# Revit family: UNB_Specchio_Multiproduct_BIM_IT_T3339;T3340;T3341;T3342;T3343;T3344_NEW
name_source: partatom
category: Plumbing Fixtures
revit_build: Autodesk Revit 2017 (Build: 20160225_1515(x64)
units: mm (PartAtom-declared; Revit-internal decimal feet)

## family parameters
Cut with Voids When Loaded = No
Host = Face
Part Type = Normal
Room Calculation Point = No
Round Connector Dimension = Use Diameter
Shared = No

## types (6) — shared parameters
Accessori = http://www.idealstandard.it
AltezzaNominale = 700 mm  [stored 2.29659 ft]
Autore = Ideal Standard
Brand = Ideal Standard
CodiceDiPrestazione = EN
Colore = specchio
Connessione = piombatura
Default Elevation = 1500 mm  [stored 4.92126 ft]
DescrizioneClassifcazioneUni2015 = Bathroom furniture
Finitura = specchio
Forma = rettangolare
Garanzia = garanzia del produttore
IfcEsportaCome = BATHROOM FURNITURE
InformazioniDiProdotto = http://www.idealstandard.it
InstruzioniInstallazione = http://www.idealstandard.it
LunghezzaNominale = 26 mm
Materiale = bicchiere
PartiDiRicambio = http://www.idealstandard.it
ProfonditàNominale = 26 mm
Revisione = 1
RiferimentoClassificazioneUni2015 = MIRRORS
Spazio = interno
Telefono = 800 652 290
TipoDiDato = Fisso
TipoEspotazioneIfc = IfcFurnitureType
TipologiaVaso = Altro
URL = http://www.idealstandard.it
UnitàDurata = anno
UnitàDurataGaranzia = anno
UnitàLineare = millimetro
UnitàMonetaria = €
UnitàSuperficie = millimetro
UnitàVolume = litro
Versione = 1
VersioneClassificazioneUni2015 = IfcFurnitureType
zero-valued in all types: Cost, CostoDiSostituzione

## per-type parameters (varying)
| type | Caratteristiche | CodiceABarre | Description | LarghezzaNominale | Model | ModelloDiRiferimento | Nome | NomeOggettoBim | NumeroDiModello | PesoNetto | Riferimento |
| T3341 - 700 x 700 mirror | SPECCHIO MID LIGHT 70X70 29,3W 230W | 8014140447337 | SPECCHIO MID LIGHT 70X70 29,3W 230W | 700 mm  [stored 2.29659 ft] | T3341BH | SPECCHIO MID LIGHT 70X70 29,3W 230W | ISI_IdealStandard_Specchio_T3341 | ISI_IdealStandard_Specchio_T3341 | T3341BH | 6.57 Kg | T3341 |
| T3339 - 500 x 700 mirror | SPECCHIO MID LIGHT 50X70 25,5W 230W | 8014140447313 | SPECCHIO MID LIGHT 50X70 25,5W 230W | 500 mm | T3339BH | SPECCHIO MID LIGHT 50X70 25,5W 230W | ISI_IdealStandard_Specchio_T3339 | ISI_IdealStandard_Specchio_T3339 | T3339BH | 5.13 Kg | T3339 |
| T3340 - 600 x 700 mirror | SPECCHIO MID LIGHT 60X70 27,4W 230W | 8014140447320 | SPECCHIO MID LIGHT 60X70 27,4W 230W | 600 mm | T3340BH | SPECCHIO MID LIGHT 60X70 27,4W 230W | ISI_IdealStandard_Specchio_T3340 | ISI_IdealStandard_Specchio_T3340 | T3340BH | 5.86 Kg | T3340 |
| T3342 - 800 x 700 mirror | SPECCHIO MID LIGHT 80X70 31,3W 230W | 8014140447344 | SPECCHIO MID LIGHT 80X70 31,3W 230W | 800 mm  [stored 2.62467 ft] | T3342BH | SPECCHIO MID LIGHT 80X70 31,3W 230W | ISI_IdealStandard_Specchio_T3342 | ISI_IdealStandard_Specchio_T3342 | T3342BH | 7.33 Kg | T3342 |
| T3343 - 1000 x 700 mirror | SPECCHIO MID LIGHT 100X70 57,1W 230W | 8014140447351 | SPECCHIO MID LIGHT 100X70 57,1W 230W | 1000 mm  [stored 3.28084 ft] | T3343BH | SPECCHIO MID LIGHT 100X70 57,1W 230W | ISI_IdealStandard_Specchio_T3343 | ISI_IdealStandard_Specchio_T3343 | T3343BH | 8.88 Kg | T3343 |
| T3344 - 1200 x 700 mirror | SPECCHIO MID LIGHT 120X70 60,9W 230W | 8014140447368 | SPECCHIO MID LIGHT 120X70 60,9W 230W | 1200 mm  [stored 3.93701 ft] | T3344BH | SPECCHIO MID LIGHT 120X70 60,9W 230W | ISI_IdealStandard_Specchio_T3344 | ISI_IdealStandard_Specchio_T3344 | T3344BH | 10.37 Kg | T3344 |

note: [stored X ft] marks values corroborated as IEEE doubles in the binary element streams (Revit-internal decimal feet)

## geometry (parser evidence)
native form markers: Sweep x1
no freeform markers — native parametric forms only
